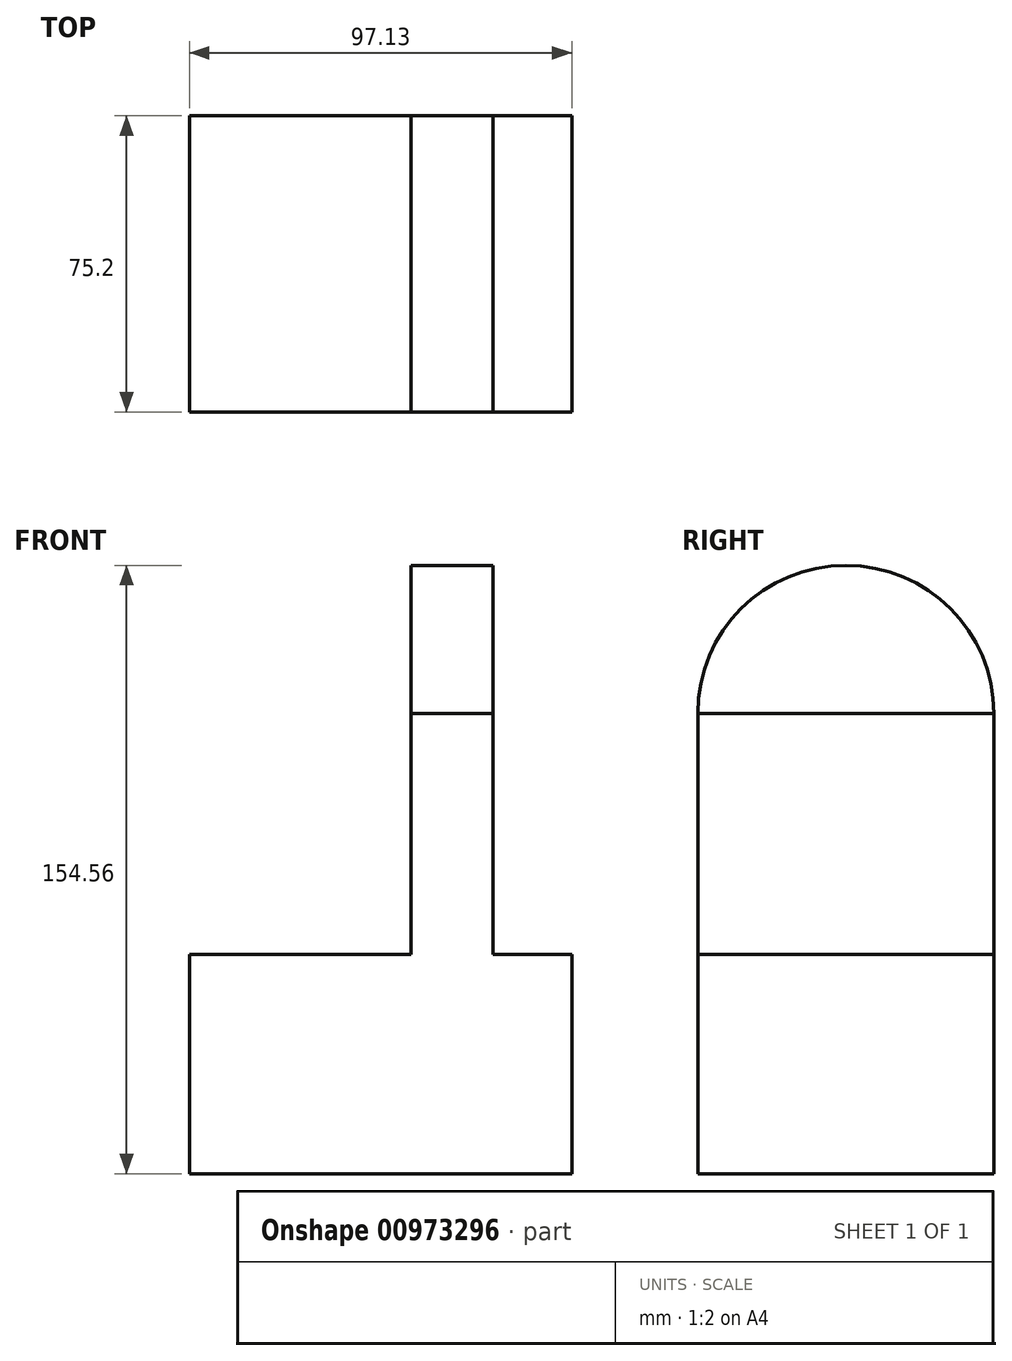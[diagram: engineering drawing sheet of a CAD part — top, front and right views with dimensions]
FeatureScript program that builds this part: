
annotation { "Feature Type Name" : "Feature", "Feature Type Description" : "" }
export const myFeature = defineFeature(function(context is Context, id is Id, definition is map)
    precondition{}
    {
        {
            var Q0;
            Q0=qCreatedBy(makeId("Top.planeOp"),FACE);
            var sketch = newSketch(context, id + "F0", { "sketchPlane" : qUnion([Q0])});
            skLineSegment(sketch, "E0.bottom", {"start": v(-41.43, 37.12) * mm, "end": v(55.7, 37.12) * mm});
            skLineSegment(sketch, "E0.top", {"start": v(-41.43, -38.08) * mm, "end": v(55.7, -38.08) * mm});
            skLineSegment(sketch, "E0.left", {"start": v(-41.43, 37.12) * mm, "end": v(-41.43, -38.08) * mm});
            skLineSegment(sketch, "E0.right", {"start": v(55.7, 37.12) * mm, "end": v(55.7, -38.08) * mm});
            skSolve(sketch);
        }
        {
            var Q0;
            Q0=makeQuery(id+"F0.imprint","IMPRINT",FACE,{"disambiguationData":[TD([[makeQuery(id+"F0.imprint","IMPRINT",EDGE,{"derivedFrom":sQuery(id+"F0.wireOp",EDGE,"E0.bottom")}),-1.0]])]});
            extrude(context, id + "F1", {"entities" : qUnion([Q0]), "depth" : 55.67 * mm, "offsetDistance" : 25.4 * mm});
        }
        {
            var Q0;
            Q0=makeQuery(id+"F1.opExtrude","CAP_FACE",FACE,{"disambiguationData":[OSD([sQuery(id+"F0.wireOp",EDGE,"E0.bottom"),sQuery(id+"F0.wireOp",EDGE,"E0.top"),sQuery(id+"F0.wireOp",EDGE,"E0.left"),sQuery(id+"F0.wireOp",EDGE,"E0.right")])],"isStart":false});
            var sketch = newSketch(context, id + "F2", { "sketchPlane" : qUnion([Q0])});
            skLineSegment(sketch, "E1", {"start": v(35.65, 37.12) * mm, "end": v(35.65, -38.08) * mm});
            skLineSegment(sketch, "E2", {"start": v(14.82, 37.12) * mm, "end": v(14.82, -38.08) * mm});
            skPoint(sketch, "E2.endSnap0", {"position": v(7.13, -38.08) * mm});
            skSolve(sketch);
        }
        {
            var Q0;
            {var subQ0=sQuery(id+"F2.wireOp",EDGE,"E1");Q0=makeQuery(id+"F2.imprint","IMPRINT",FACE,{"disambiguationData":[TD([[makeQuery(id+"F2.imprint","IMPRINT",EDGE,{"derivedFrom":subQ0}),-1.0]])]});}
            extrude(context, id + "F3", {"entities" : qUnion([Q0]), "operationType" : NewBodyOperationType.ADD, "depth" : 61.3 * mm, "offsetDistance" : 25.4 * mm});
        }
        {
            var Q0;
            Q0=makeQuery(id+"F3.opExtrude","SWEPT_FACE",FACE,{"disambiguationData":[OSD([sQuery(id+"F2.wireOp",EDGE,"E2")])]});
            var sketch = newSketch(context, id + "F4", { "sketchPlane" : qUnion([Q0])});
            skArc(sketch, "E3", {"start": v(38.08, 116.96) * mm, "mid": v(0.48, 154.56) * mm, "end": v(-37.12, 116.96) * mm});
            skSolve(sketch);
        }
        {
            var Q0;
            Q0=makeQuery(id+"F4.imprint","IMPRINT",FACE,{"disambiguationData":[TD([[makeQuery(id+"F4.imprint","IMPRINT",EDGE,{"derivedFrom":sQuery(id+"F4.wireOp",EDGE,"E3")}),1.0]])]});
            extrude(context, id + "F5", {"entities" : qUnion([Q0]), "oppositeDirection" : true, "depth" : 20.83 * mm, "offsetDistance" : 25.4 * mm});
        }
    });
